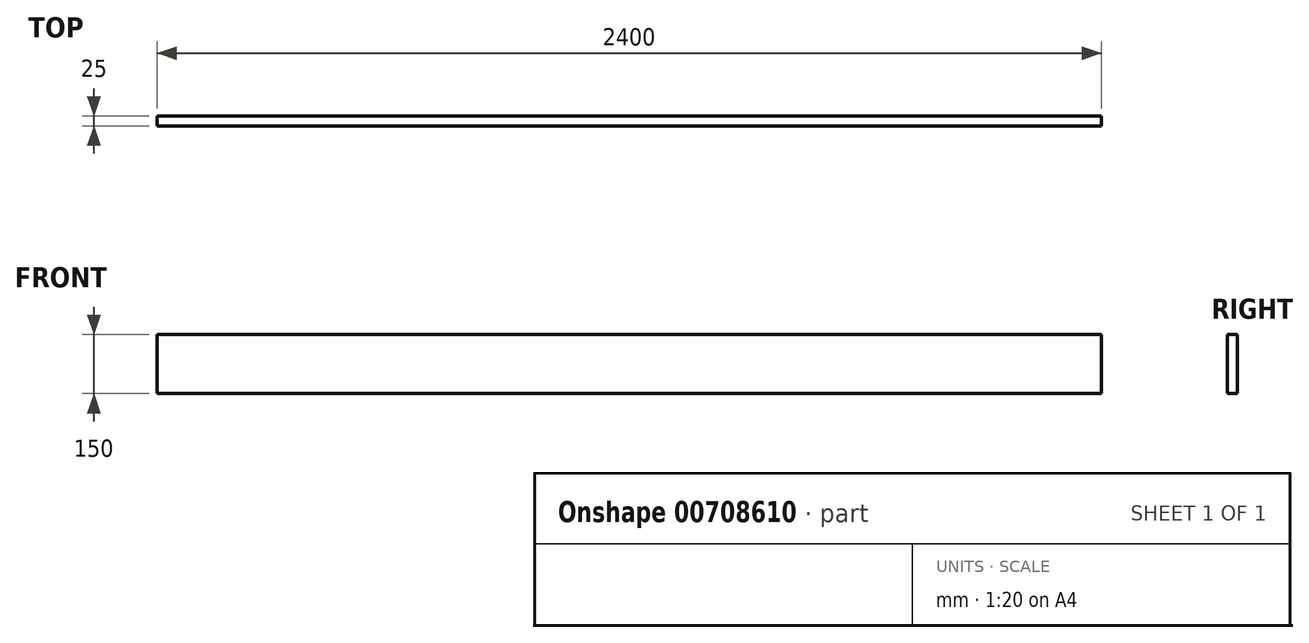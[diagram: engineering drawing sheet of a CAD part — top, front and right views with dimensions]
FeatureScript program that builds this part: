
annotation { "Feature Type Name" : "Feature", "Feature Type Description" : "" }
export const myFeature = defineFeature(function(context is Context, id is Id, definition is map)
    precondition{}
    {
        {
            var Q0;
            Q0=qCreatedBy(makeId("Front.planeOp"),FACE);
            var sketch = newSketch(context, id + "F0", { "sketchPlane" : qUnion([Q0])});
            skLineSegment(sketch, "E0.bottom", {"start": v(0, 0) * mm, "end": v(2400, 0) * mm});
            skLineSegment(sketch, "E0.top", {"start": v(0, 150) * mm, "end": v(2400, 150) * mm});
            skLineSegment(sketch, "E0.left", {"start": v(0, 0) * mm, "end": v(0, 150) * mm});
            skLineSegment(sketch, "E0.right", {"start": v(2400, 0) * mm, "end": v(2400, 150) * mm});
            skSolve(sketch);
        }
        {
            var Q0;
            Q0=makeQuery(id+"F0.imprint","IMPRINT",FACE,{"disambiguationData":[TD([[makeQuery(id+"F0.imprint","IMPRINT",EDGE,{"derivedFrom":sQuery(id+"F0.wireOp",EDGE,"E0.bottom")}),1.0]])]});
            extrude(context, id + "F1", {"entities" : qUnion([Q0]), "depth" : 25 * mm, "offsetDistance" : 25 * mm});
        }
    });
